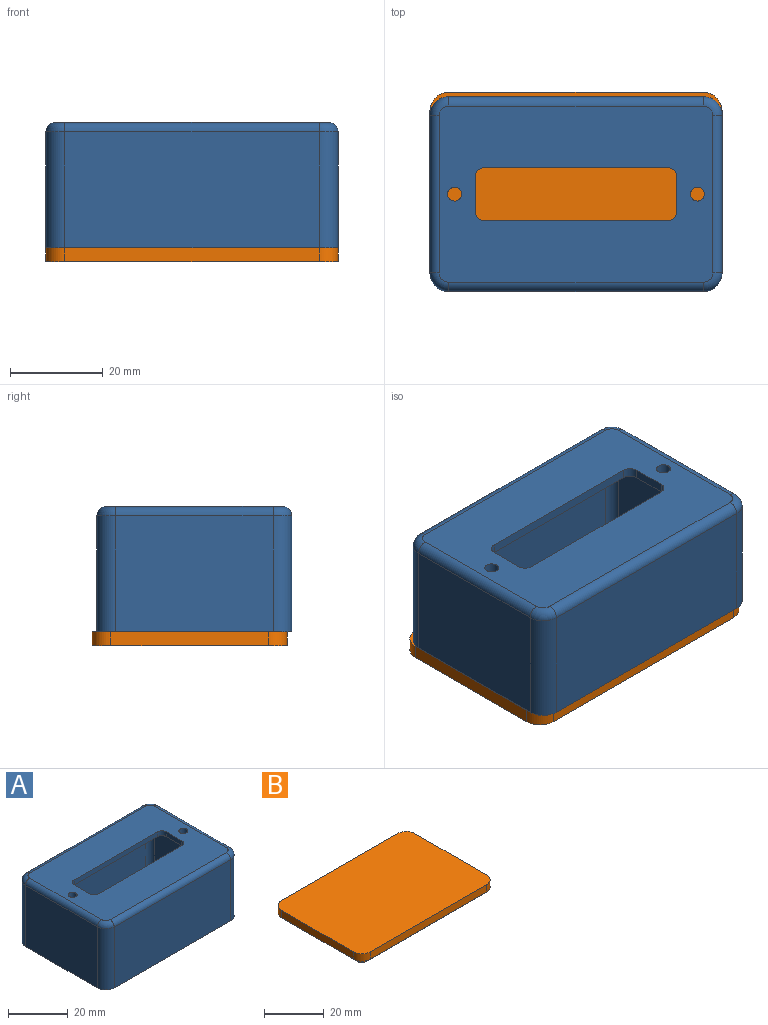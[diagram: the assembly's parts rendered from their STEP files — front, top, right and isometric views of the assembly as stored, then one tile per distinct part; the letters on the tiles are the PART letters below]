
ASSEMBLY  parts=2 mates=1
PART A: 53 faces, bbox 63.7x42.7x27 mm
  f0: plane 55x25mm, normal (0,-1,0), area 1375mm2, adj f20,f25,f28,f34
  f1: plane 34x25mm, normal (1,0,0), area 850mm2, adj f20,f25,f26,f35
  f2: plane 55x25mm, normal (0,1,0), area 1375mm2, adj f20,f26,f27,f31
  f3: cylinder r=2mm len=2mm, axis (0,0,-1), area 6.3mm2, adj f4,f12,f14,f15
  f4: plane 39.5x2mm, normal (0,-1,0), area 79mm2, adj f3,f5,f14,f15
  f5: cylinder r=2mm len=2mm, axis (0,0,-1), area 6.3mm2, adj f4,f6,f14,f15
  f6: plane 7.5x2mm, normal (-1,0,0), area 15mm2, adj f5,f7,f14,f15
  f7: cylinder r=2mm len=2mm, axis (0,0,-1), area 6.3mm2, adj f6,f8,f14,f15
  f8: plane 39.5x2mm, normal (0,1,0), area 79mm2, adj f7,f9,f14,f15
  f9: cylinder r=2mm len=2mm, axis (0,0,-1), area 6.3mm2, adj f8,f12,f14,f15
  f10: cylinder r=1.5mm len=3mm, axis (0,0,-1), area 18.8mm2, adj f14,f15
  f11: cylinder r=1.5mm len=3mm, axis (0,0,-1), area 18.8mm2, adj f14,f15
  f12: plane 7.5x2mm, normal (1,0,0), area 15mm2, adj f3,f9,f14,f15
  f13: plane 34x25mm, normal (-1,0,0), area 850mm2, adj f20,f27,f28,f30
  f14: plane 59x38mm, normal (0,0,1), area 1727.6mm2, adj f3,f4,f5,f6,f7,f8,f9,f10
  f15: plane 57x36mm, normal (0,0,-1), area 1540.2mm2, adj f3,f4,f5,f6,f7,f8,f9,f10
  f16: plane 55x22mm, normal (0,1,0), area 1210mm2, adj f21,f24,f43,f51
  f17: plane 34x22mm, normal (-1,0,0), area 748mm2, adj f21,f22,f42,f47
  f18: plane 55x22mm, normal (0,-1,0), area 1210mm2, adj f22,f23,f38,f46
  f19: plane 34x22mm, normal (1,0,0), area 748mm2, adj f23,f24,f39,f50
  f20: plane 63x42mm, normal (0,0,-1), area 200mm2, adj f0,f1,f2,f13,f25,f26,f27,f28
  f21: cylinder r=2mm len=22mm, axis (0,0,1), area 69.1mm2, adj f16,f17,f44,f49
  f22: cylinder r=2mm len=22mm, axis (0,0,-1), area 69.1mm2, adj f17,f18,f40,f45
  f23: cylinder r=2mm len=22mm, axis (0,0,1), area 69.1mm2, adj f18,f19,f37,f48
  f24: cylinder r=2mm len=22mm, axis (0,0,-1), area 69.1mm2, adj f16,f19,f41,f52
  f25: cylinder r=4mm len=25mm, axis (0,0,1), area 157.1mm2, adj f0,f1,f20,f36
  f26: cylinder r=4mm len=25mm, axis (0,0,-1), area 157.1mm2, adj f1,f2,f20,f33
  f27: cylinder r=4mm len=25mm, axis (0,0,1), area 157.1mm2, adj f2,f13,f20,f29
  f28: cylinder r=4mm len=25mm, axis (0,0,-1), area 157.1mm2, adj f0,f13,f20,f32
  f29: torus R=2mm, axis (0,0,1), area 16.2mm2, adj f14,f27,f30,f31
  f30: cylinder r=2mm len=34mm, axis (0,1,0), area 106.8mm2, adj f13,f14,f29,f32
  f31: cylinder r=2mm len=55mm, axis (1,0,0), area 172.8mm2, adj f2,f14,f29,f33
  f32: torus R=2mm, axis (0,0,1), area 16.2mm2, adj f14,f28,f30,f34
  f33: torus R=2mm, axis (0,0,1), area 16.2mm2, adj f14,f26,f31,f35
  f34: cylinder r=2mm len=55mm, axis (-1,0,0), area 172.8mm2, adj f0,f14,f32,f36
  f35: cylinder r=2mm len=34mm, axis (0,-1,0), area 106.8mm2, adj f1,f14,f33,f36
  f36: torus R=2mm, axis (0,0,1), area 16.2mm2, adj f14,f25,f34,f35
  f37: torus R=1mm, axis (0,0,1), area 4mm2, adj f15,f23,f38,f39
  f38: cylinder r=1mm len=55mm, axis (1,0,0), area 86.4mm2, adj f15,f18,f37,f40
  f39: cylinder r=1mm len=34mm, axis (0,1,0), area 53.4mm2, adj f15,f19,f37,f41
  f40: torus R=1mm, axis (0,0,1), area 4mm2, adj f15,f22,f38,f42
  f41: torus R=1mm, axis (0,0,1), area 4mm2, adj f15,f24,f39,f43
  f42: cylinder r=1mm len=34mm, axis (0,-1,0), area 53.4mm2, adj f15,f17,f40,f44
  f43: cylinder r=1mm len=55mm, axis (-1,0,0), area 86.4mm2, adj f15,f16,f41,f44
  f44: torus R=1mm, axis (0,0,1), area 4mm2, adj f15,f21,f42,f43
  f45: cone r=3mm half-angle=26.6deg, axis (0,0,-1), area 8.8mm2, adj f20,f22,f46,f47
  f46: plane 55x2mm, normal (0,-0.89,-0.45), area 123mm2, adj f18,f20,f45,f48
  f47: plane 34x2mm, normal (-0.89,0,-0.45), area 76mm2, adj f17,f20,f45,f49
  f48: cone r=3mm half-angle=26.6deg, axis (0,0,-1), area 8.8mm2, adj f20,f23,f46,f50
  f49: cone r=3mm half-angle=26.6deg, axis (0,0,-1), area 8.8mm2, adj f20,f21,f47,f51
  f50: plane 34x2mm, normal (0.89,0,-0.45), area 76mm2, adj f19,f20,f48,f52
  f51: plane 55x2mm, normal (0,0.89,-0.45), area 123mm2, adj f16,f20,f49,f52
  f52: cone r=3mm half-angle=26.6deg, axis (0,0,-1), area 8.8mm2, adj f20,f24,f50,f51
PART B: 19 faces, bbox 63x42x5 mm
  f0: cylinder r=4mm len=4mm, axis (0,0,1), area 18.8mm2, adj f1,f7,f8,f9
  f1: plane 34x3mm, normal (1,0,0), area 102mm2, adj f0,f2,f8,f9
  f2: cylinder r=4mm len=4mm, axis (0,0,1), area 18.8mm2, adj f1,f3,f8,f9
  f3: plane 55x3mm, normal (0,-1,0), area 165mm2, adj f2,f4,f8,f9
  f4: cylinder r=4mm len=4mm, axis (0,0,1), area 18.8mm2, adj f3,f5,f8,f9
  f5: plane 34x3mm, normal (-1,0,0), area 102mm2, adj f4,f6,f8,f9
  f6: cylinder r=4mm len=4mm, axis (0,0,1), area 18.8mm2, adj f5,f7,f8,f9
  f7: plane 55x3mm, normal (0,1,0), area 165mm2, adj f0,f6,f8,f9
  f8: plane 63x42mm, normal (0,0,-1), area 393.7mm2, adj f0,f1,f2,f3,f4,f5,f6,f7
  f9: plane 63x42mm, normal (0,0,1), area 2632.3mm2, adj f0,f1,f2,f3,f4,f5,f6,f7
  f10: cylinder r=2mm len=2mm, axis (0,0,1), area 6.3mm2, adj f8,f11,f17,f18
  f11: plane 55x2mm, normal (0,-1,0), area 110mm2, adj f8,f10,f12,f18
  f12: cylinder r=2mm len=2mm, axis (0,0,1), area 6.3mm2, adj f8,f11,f13,f18
  f13: plane 34x2mm, normal (-1,0,0), area 68mm2, adj f8,f12,f14,f18
  f14: cylinder r=2mm len=2mm, axis (0,0,1), area 6.3mm2, adj f8,f13,f15,f18
  f15: plane 55x2mm, normal (0,1,0), area 110mm2, adj f8,f14,f16,f18
  f16: cylinder r=2mm len=2mm, axis (0,0,1), area 6.3mm2, adj f8,f15,f17,f18
  f17: plane 34x2mm, normal (1,0,0), area 68mm2, adj f8,f10,f16,f18
  f18: plane 59x38mm, normal (0,0,-1), area 2238.6mm2, adj f10,f11,f12,f13,f14,f15,f16,f17
PLACE A t=(-10.54,13.02,18.32)mm
PLACE B rot(axis=(0,-1,0),180deg) t=(-10.54,14.02,-59.68)mm fixed
MATE slider B.f8 <-> A.f20  axis (0,0,1) through (-10.54,-6.98,-6.68)mm
